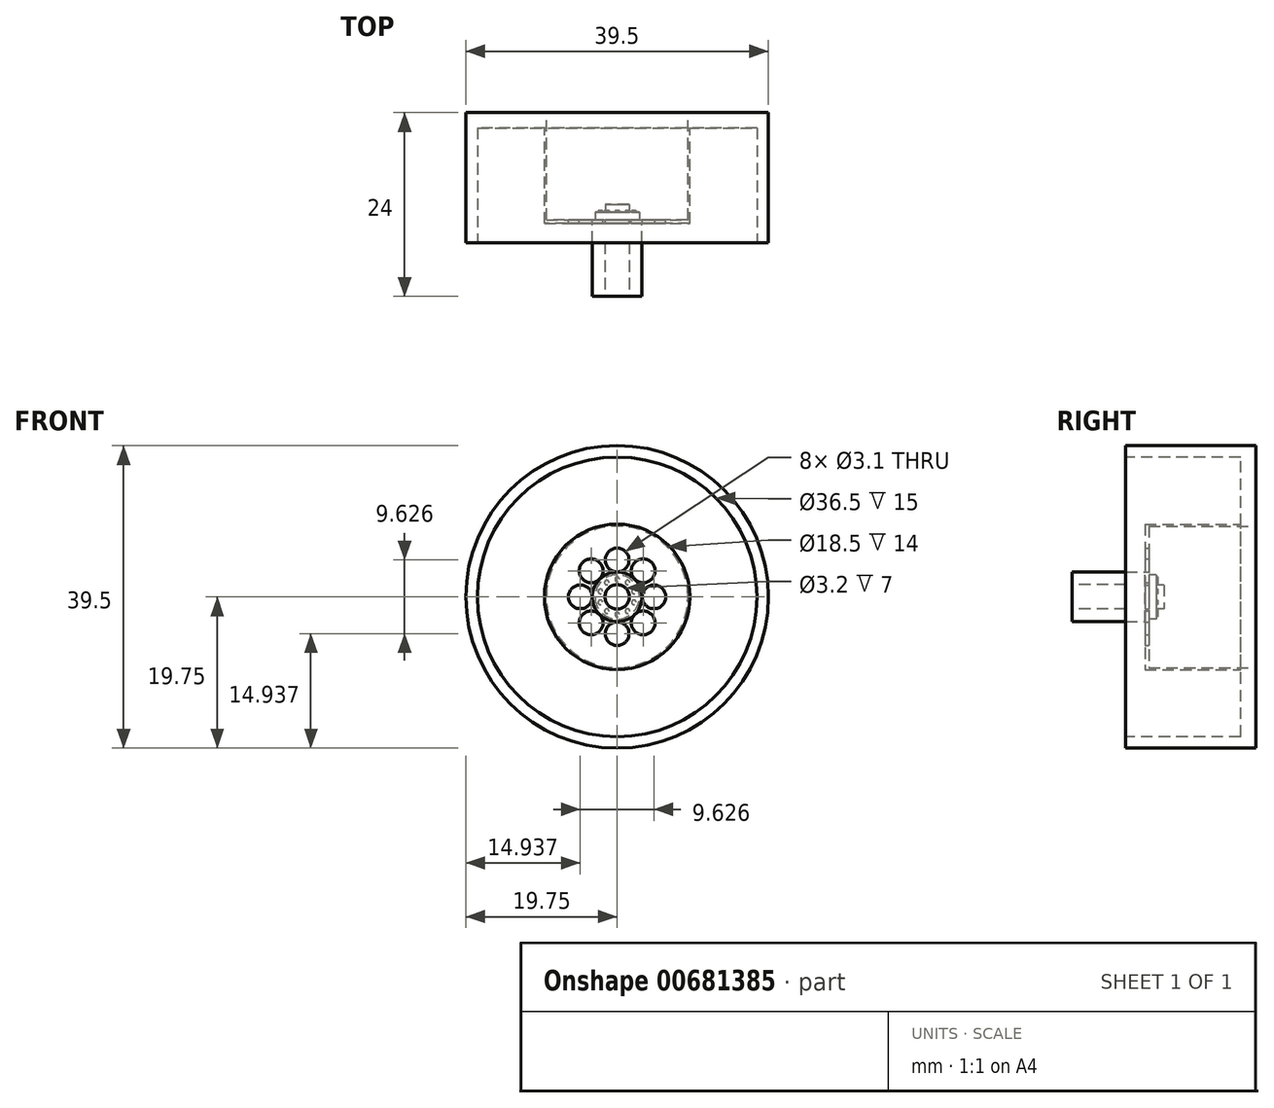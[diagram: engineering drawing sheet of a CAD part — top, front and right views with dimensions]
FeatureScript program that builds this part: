
annotation { "Feature Type Name" : "Feature", "Feature Type Description" : "" }
export const myFeature = defineFeature(function(context is Context, id is Id, definition is map)
    precondition{}
    {
        {
            var Q0;
            Q0=qCreatedBy(makeId("Front.planeOp"),FACE);
            var sketch = newSketch(context, id + "F0", { "sketchPlane" : qUnion([Q0])});
            skCircle(sketch, "E0", {"center": v(0, 0) * mm, "radius": 19.75 * mm});
            skSolve(sketch);
        }
        {
            var Q0;
            Q0=makeQuery(id+"F0.imprint","IMPRINT",FACE,{"disambiguationData":[TD([[makeQuery(id+"F0.imprint","IMPRINT",EDGE,{"derivedFrom":sQuery(id+"F0.wireOp",EDGE,"E0")}),1.0]])]});
            extrude(context, id + "F1", {"entities" : qUnion([Q0]), "depth" : 17 * mm, "offsetDistance" : 25.4 * mm});
        }
        {
            var Q0;
            Q0=makeQuery(id+"F1.opExtrude","CAP_FACE",FACE,{"disambiguationData":[OSD([sQuery(id+"F0.wireOp",EDGE,"E0")])],"isStart":false});
            var sketch = newSketch(context, id + "F2", { "sketchPlane" : qUnion([Q0])});
            skCircle(sketch, "E1", {"center": v(0, 0) * mm, "radius": 18.25 * mm});
            skSolve(sketch);
        }
        {
            var Q0;
            Q0=makeQuery(id+"F2.imprint","IMPRINT",FACE,{"disambiguationData":[TD([[makeQuery(id+"F2.imprint","IMPRINT",EDGE,{"derivedFrom":sQuery(id+"F2.wireOp",EDGE,"E1")}),1.0]])]});
            extrude(context, id + "F3", {"entities" : qUnion([Q0]), "operationType" : NewBodyOperationType.REMOVE, "oppositeDirection" : true, "depth" : 15 * mm, "offsetDistance" : 25.4 * mm});
        }
        {
            var Q0;
            Q0=makeQuery(id+"F1.opExtrude","CAP_FACE",FACE,{"disambiguationData":[OSD([sQuery(id+"F0.wireOp",EDGE,"E0")])],"isStart":true});
            var sketch = newSketch(context, id + "F4", { "sketchPlane" : qUnion([Q0])});
            skCircle(sketch, "E2", {"center": v(0, 0) * mm, "radius": 9.5 * mm});
            skSolve(sketch);
        }
        {
            var Q0;
            Q0=makeQuery(id+"F4.imprint","IMPRINT",FACE,{"disambiguationData":[TD([[makeQuery(id+"F4.imprint","IMPRINT",EDGE,{"derivedFrom":sQuery(id+"F4.wireOp",EDGE,"E2")}),1.0]])]});
            extrude(context, id + "F5", {"entities" : qUnion([Q0]), "operationType" : NewBodyOperationType.ADD, "oppositeDirection" : true, "depth" : 14.5 * mm, "offsetDistance" : 25.4 * mm});
        }
        {
            var Q0;
            Q0=makeQuery(id+"F1.opExtrude","CAP_FACE",FACE,{"disambiguationData":[OSD([sQuery(id+"F0.wireOp",EDGE,"E0")])],"isStart":true});
            var sketch = newSketch(context, id + "F6", { "sketchPlane" : qUnion([Q0])});
            skCircle(sketch, "E3", {"center": v(0, 0) * mm, "radius": 9.25 * mm});
            skSolve(sketch);
        }
        {
            var Q0;
            Q0 = qSketchRegion(id + "F6", true);
            extrude(context, id + "F7", {"entities" : qUnion([Q0]), "operationType" : NewBodyOperationType.REMOVE, "oppositeDirection" : true, "depth" : 14 * mm, "offsetDistance" : 25.4 * mm});
        }
        {
            var Q0;
            Q0=makeQuery(id+"F5.opExtrude","CAP_FACE",FACE,{"disambiguationData":[OSD([sQuery(id+"F4.wireOp",EDGE,"E2")])],"isStart":false});
            var sketch = newSketch(context, id + "F8", { "sketchPlane" : qUnion([Q0])});
            skCircle(sketch, "E4", {"center": v(0, 0) * mm, "radius": 3.25 * mm});
            skSolve(sketch);
        }
        {
            var Q0;
            Q0 = qSketchRegion(id + "F8", true);
            extrude(context, id + "F9", {"entities" : qUnion([Q0]), "operationType" : NewBodyOperationType.ADD, "depth" : 9.5 * mm, "offsetDistance" : 25.4 * mm});
        }
        {
            var Q0;
            Q0=makeQuery(id+"F9.opExtrude","CAP_FACE",FACE,{"disambiguationData":[OSD([sQuery(id+"F8.wireOp",EDGE,"E4")])],"isStart":false});
            var sketch = newSketch(context, id + "F10", { "sketchPlane" : qUnion([Q0])});
            skCircle(sketch, "E5", {"center": v(0, 0) * mm, "radius": 1.6 * mm});
            skSolve(sketch);
        }
        {
            var Q0;
            Q0 = qSketchRegion(id + "F10", true);
            extrude(context, id + "F11", {"entities" : qUnion([Q0]), "operationType" : NewBodyOperationType.REMOVE, "oppositeDirection" : true, "depth" : 7 * mm, "offsetDistance" : 25.4 * mm});
        }
        {
            var Q0;
            Q0=makeQuery(id+"F7.boolean.opBoolean","COPY",FACE,{"derivedFrom":makeQuery(id+"F7.opExtrude","CAP_FACE",FACE,{"disambiguationData":[OSD([sQuery(id+"F6.wireOp",EDGE,"E3")])],"isStart":false})});
            var sketch = newSketch(context, id + "F12", { "sketchPlane" : qUnion([Q0])});
            skCircle(sketch, "E6", {"center": v(0, 4.81) * mm, "radius": 1.55 * mm});
            skCircle(sketch, "E7.1.0", {"center": v(-3.4, 3.4) * mm, "radius": 1.55 * mm});
            skCircle(sketch, "E7.2.0", {"center": v(-4.81, 0) * mm, "radius": 1.55 * mm});
            skCircle(sketch, "E7.3.0", {"center": v(-3.4, -3.4) * mm, "radius": 1.55 * mm});
            skCircle(sketch, "E7.4.0", {"center": v(0, -4.81) * mm, "radius": 1.55 * mm});
            skCircle(sketch, "E7.5.0", {"center": v(3.4, -3.4) * mm, "radius": 1.55 * mm});
            skCircle(sketch, "E7.6.0", {"center": v(4.81, 0) * mm, "radius": 1.55 * mm});
            skCircle(sketch, "E7.7.0", {"center": v(3.4, 3.4) * mm, "radius": 1.55 * mm});
            skPoint(sketch, "E7.center", {"position": v(0, 0) * mm});
            skSolve(sketch);
        }
        {
            var Q0;
            Q0=makeQuery(id+"F12.imprint","IMPRINT",FACE,{"disambiguationData":[TD([[makeQuery(id+"F12.imprint","IMPRINT",EDGE,{"derivedFrom":sQuery(id+"F12.wireOp",EDGE,"E6")}),1.0]])]});
            extrude(context, id + "F13", {"entities" : qUnion([Q0]), "operationType" : NewBodyOperationType.REMOVE, "oppositeDirection" : true, "depth" : 25.4 * mm, "offsetDistance" : 25.4 * mm});
        }
        {
            var Q0;
            Q0=makeQuery(id+"F12.imprint","IMPRINT",FACE,{"disambiguationData":[TD([[makeQuery(id+"F12.imprint","IMPRINT",EDGE,{"derivedFrom":sQuery(id+"F12.wireOp",EDGE,"E7.1.0")}),1.0]])]});
            var Q1;
            Q1=makeQuery(id+"F12.imprint","IMPRINT",FACE,{"disambiguationData":[TD([[makeQuery(id+"F12.imprint","IMPRINT",EDGE,{"derivedFrom":sQuery(id+"F12.wireOp",EDGE,"E7.2.0")}),1.0]])]});
            var Q2;
            Q2=makeQuery(id+"F12.imprint","IMPRINT",FACE,{"disambiguationData":[TD([[makeQuery(id+"F12.imprint","IMPRINT",EDGE,{"derivedFrom":sQuery(id+"F12.wireOp",EDGE,"E7.3.0")}),1.0]])]});
            var Q3;
            Q3=makeQuery(id+"F12.imprint","IMPRINT",FACE,{"disambiguationData":[TD([[makeQuery(id+"F12.imprint","IMPRINT",EDGE,{"derivedFrom":sQuery(id+"F12.wireOp",EDGE,"E7.4.0")}),1.0]])]});
            var Q4;
            Q4=makeQuery(id+"F12.imprint","IMPRINT",FACE,{"disambiguationData":[TD([[makeQuery(id+"F12.imprint","IMPRINT",EDGE,{"derivedFrom":sQuery(id+"F12.wireOp",EDGE,"E7.5.0")}),1.0]])]});
            var Q5;
            Q5=makeQuery(id+"F12.imprint","IMPRINT",FACE,{"disambiguationData":[TD([[makeQuery(id+"F12.imprint","IMPRINT",EDGE,{"derivedFrom":sQuery(id+"F12.wireOp",EDGE,"E7.6.0")}),1.0]])]});
            var Q6;
            Q6=makeQuery(id+"F12.imprint","IMPRINT",FACE,{"disambiguationData":[TD([[makeQuery(id+"F12.imprint","IMPRINT",EDGE,{"derivedFrom":sQuery(id+"F12.wireOp",EDGE,"E7.7.0")}),1.0]])]});
            extrude(context, id + "F14", {"entities" : qUnion([Q0, Q1, Q2, Q3, Q4, Q5, Q6]), "operationType" : NewBodyOperationType.REMOVE, "oppositeDirection" : true, "depth" : 25.4 * mm, "offsetDistance" : 25.4 * mm});
        }
        {
            var Q0;
            Q0=makeQuery(id+"F12.imprint","IMPRINT",FACE,{"disambiguationData":[TD([[makeQuery(id+"F12.imprint","IMPRINT",EDGE,{"derivedFrom":sQuery(id+"F12.wireOp",EDGE,"E6")}),-1.0]])]});
            var sketch = newSketch(context, id + "F15", { "sketchPlane" : qUnion([Q0])});
            skCircle(sketch, "E8", {"center": v(0, 0) * mm, "radius": 2.9 * mm});
            skSolve(sketch);
        }
        {
            var Q0;
            Q0=makeQuery(id+"F15.imprint","IMPRINT",FACE,{"disambiguationData":[TD([[makeQuery(id+"F15.imprint","IMPRINT",EDGE,{"derivedFrom":sQuery(id+"F15.wireOp",EDGE,"E8")}),1.0]])]});
            extrude(context, id + "F16", {"entities" : qUnion([Q0]), "operationType" : NewBodyOperationType.ADD, "depth" : 1 * mm, "offsetDistance" : 25.4 * mm});
        }
        {
            var Q0;
            Q0=makeQuery(id+"F16.opExtrude","CAP_FACE",FACE,{"disambiguationData":[OSD([sQuery(id+"F15.wireOp",EDGE,"E8")])],"isStart":false});
            var sketch = newSketch(context, id + "F17", { "sketchPlane" : qUnion([Q0])});
            skCircle(sketch, "E9", {"center": v(0, 0) * mm, "radius": 1.55 * mm});
            skSolve(sketch);
        }
        {
            var Q0;
            Q0=makeQuery(id+"F17.imprint","IMPRINT",FACE,{"disambiguationData":[TD([[makeQuery(id+"F17.imprint","IMPRINT",EDGE,{"derivedFrom":sQuery(id+"F17.wireOp",EDGE,"E9")}),1.0]])]});
            extrude(context, id + "F18", {"entities" : qUnion([Q0]), "operationType" : NewBodyOperationType.ADD, "depth" : 1 * mm, "offsetDistance" : 25.4 * mm});
        }
        {
            var Q0;
            Q0=makeQuery(id+"F16.opExtrude","CAP_FACE",FACE,{"disambiguationData":[OSD([sQuery(id+"F15.wireOp",EDGE,"E8")])],"isStart":false});
            var sketch = newSketch(context, id + "F19", { "sketchPlane" : qUnion([Q0])});
            skCircle(sketch, "E10", {"center": v(0, 2.3) * mm, "radius": 0.3 * mm});
            skCircle(sketch, "E11.1.0", {"center": v(-1.35, 1.86) * mm, "radius": 0.3 * mm});
            skCircle(sketch, "E11.2.0", {"center": v(-2.19, 0.71) * mm, "radius": 0.3 * mm});
            skCircle(sketch, "E11.3.0", {"center": v(-2.19, -0.71) * mm, "radius": 0.3 * mm});
            skCircle(sketch, "E11.4.0", {"center": v(-1.35, -1.86) * mm, "radius": 0.3 * mm});
            skCircle(sketch, "E11.5.0", {"center": v(0, -2.3) * mm, "radius": 0.3 * mm});
            skCircle(sketch, "E11.6.0", {"center": v(1.35, -1.86) * mm, "radius": 0.3 * mm});
            skCircle(sketch, "E11.7.0", {"center": v(2.19, -0.71) * mm, "radius": 0.3 * mm});
            skCircle(sketch, "E11.8.0", {"center": v(2.19, 0.71) * mm, "radius": 0.3 * mm});
            skCircle(sketch, "E11.9.0", {"center": v(1.35, 1.86) * mm, "radius": 0.3 * mm});
            skPoint(sketch, "E11.center", {"position": v(0, 0) * mm});
            skSolve(sketch);
        }
        {
            var Q0;
            Q0=makeQuery(id+"F19.imprint","IMPRINT",FACE,{"disambiguationData":[TD([[makeQuery(id+"F19.imprint","IMPRINT",EDGE,{"derivedFrom":sQuery(id+"F19.wireOp",EDGE,"E11.1.0")}),1.0]])]});
            var Q1;
            Q1=makeQuery(id+"F19.imprint","IMPRINT",FACE,{"disambiguationData":[TD([[makeQuery(id+"F19.imprint","IMPRINT",EDGE,{"derivedFrom":sQuery(id+"F19.wireOp",EDGE,"E10")}),1.0]])]});
            var Q2;
            Q2=makeQuery(id+"F19.imprint","IMPRINT",FACE,{"disambiguationData":[TD([[makeQuery(id+"F19.imprint","IMPRINT",EDGE,{"derivedFrom":sQuery(id+"F19.wireOp",EDGE,"E11.9.0")}),1.0]])]});
            var Q3;
            Q3=makeQuery(id+"F19.imprint","IMPRINT",FACE,{"disambiguationData":[TD([[makeQuery(id+"F19.imprint","IMPRINT",EDGE,{"derivedFrom":sQuery(id+"F19.wireOp",EDGE,"E11.8.0")}),1.0]])]});
            var Q4;
            Q4=makeQuery(id+"F19.imprint","IMPRINT",FACE,{"disambiguationData":[TD([[makeQuery(id+"F19.imprint","IMPRINT",EDGE,{"derivedFrom":sQuery(id+"F19.wireOp",EDGE,"E11.7.0")}),1.0]])]});
            var Q5;
            Q5=makeQuery(id+"F19.imprint","IMPRINT",FACE,{"disambiguationData":[TD([[makeQuery(id+"F19.imprint","IMPRINT",EDGE,{"derivedFrom":sQuery(id+"F19.wireOp",EDGE,"E11.6.0")}),1.0]])]});
            var Q6;
            Q6=makeQuery(id+"F19.imprint","IMPRINT",FACE,{"disambiguationData":[TD([[makeQuery(id+"F19.imprint","IMPRINT",EDGE,{"derivedFrom":sQuery(id+"F19.wireOp",EDGE,"E11.5.0")}),1.0]])]});
            var Q7;
            Q7=makeQuery(id+"F19.imprint","IMPRINT",FACE,{"disambiguationData":[TD([[makeQuery(id+"F19.imprint","IMPRINT",EDGE,{"derivedFrom":sQuery(id+"F19.wireOp",EDGE,"E11.4.0")}),1.0]])]});
            var Q8;
            Q8=makeQuery(id+"F19.imprint","IMPRINT",FACE,{"disambiguationData":[TD([[makeQuery(id+"F19.imprint","IMPRINT",EDGE,{"derivedFrom":sQuery(id+"F19.wireOp",EDGE,"E11.3.0")}),1.0]])]});
            var Q9;
            Q9=makeQuery(id+"F19.imprint","IMPRINT",FACE,{"disambiguationData":[TD([[makeQuery(id+"F19.imprint","IMPRINT",EDGE,{"derivedFrom":sQuery(id+"F19.wireOp",EDGE,"E11.2.0")}),1.0]])]});
            extrude(context, id + "F20", {"entities" : qUnion([Q0, Q1, Q2, Q3, Q4, Q5, Q6, Q7, Q8, Q9]), "operationType" : NewBodyOperationType.ADD, "depth" : .2 * mm, "offsetDistance" : 25.4 * mm});
        }
    });
